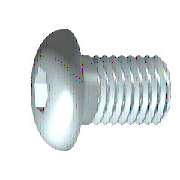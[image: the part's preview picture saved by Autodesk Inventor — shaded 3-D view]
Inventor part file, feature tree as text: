
AUTODESK INVENTOR PART (.ipt)
format: ipt  version: 2015 (Build 190159000, 159)  size: 196,608 bytes
history: native  units: mm (DEFAULTED — no unit token found)
features: sketch x2, extrude x1, plane x1, fillet x1
ambient origin geometry x7: Origin, YZ Plane, XY Plane, X Axis, Y Axis, Z Axis, Center Point
bodies: Solid1 (feature_tree), Body (feature_tree)
feature tree (5):
  extrude  "Slot"  Depth=1.8542mm
  plane  "Work Plane1"
  fillet  "Fillet2"  Radius=1.8542mm
  sketch  "Sketch1"  dims[d1=11.10976mm d2=1.59014mm d3=1.8542mm]
  sketch  "Sketch2"  dims[d4=1.1176mm d5=60.0deg d6=3.5052mm d7=3.5052mm d8=2.287693mm d9=6.6548mm d10=90.0deg d11=10.0mm d12=0.0mm d13=11.10976mm d14=0.0mm d15=0.486918mm d16=0.486918mm d17=1.6002mm d19=0.0mm d26=12.7mm d27=45.0deg d28=0.0mm d29=0.0mm d30=0.1mm]
